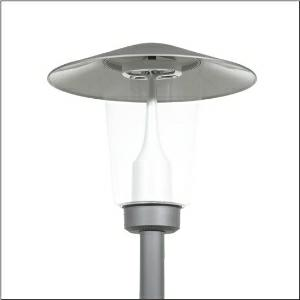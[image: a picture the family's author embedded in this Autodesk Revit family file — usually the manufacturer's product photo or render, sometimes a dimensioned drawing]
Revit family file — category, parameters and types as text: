
# Revit family: pilzleuchte_iq___st1_2a_5xa5235kf14hp_bd7e
name_source: partatom
category: Lighting Fixtures
units: mm (PartAtom-declared; Revit-internal decimal feet)

## family parameters
Cut with Voids When Loaded = No
Host = Face
Light Source = No
Part Type = Normal
Room Calculation Point = No
Round Connector Dimension = Use Diameter
Shared = No

## types (1)
- --- (1 x LED, 4990 lm, 33.6 W, 4000K)
    Apparent Load = 34 VA
    CIE Flux Codes = 23 60 92 98 100
    Color Rendering = 70
    Color Temperature = 4000K
    Default Elevation = 1800 mm
    Description = Mushroom Luminaire iQ, mast luminaire, Module 540 iQ-SR, primary light control with 3 zone facetted reflector, of plastic, silver coated, highly specular, structured, primary optical cover: cover, of PMMA, transparent, light distribution: ST1.2a, light emission: direct distribution, primary light characteristic: asymmetric, installation type: post-top, LED, High Power LED, rated luminous flux: 4.990lm, luminous efficacy: 149lm/W, light colour: 740, colour temperature: 4000K, control gear: iQ Street-Remote, control: pre-setting: logarithmic dimming characteristic, Street-Remote, Auto-Match, Temp-Guard, Lumen-Switch, Night-Set, Smart-Wire, Light-Fading, Desk-Remote (wireless, voltage-free reading and setting of iQ features in the workshop via application-optimized NFC function/RFID function), optimised constant luminous flux control (CLO 2.0), with terminal, 6-pole, max. 2.5mm², mains connection: 230..240V, AC, 50/60Hz, start of lifetime: 34W, end of service life: 36W, reduction: 15W, luminaire housing, upper part, of glass-fibre reinforced polyester, coated, Siteco® metallic grey (DB 702S), diameter: 650mm, height: 586mm, spigot size: d x l = 76 x 70mm (post-top) | with reducer (optional accessory) 60 x 70mm, mounting height: 3..5m, post-top mast mounting element, of diecast aluminium, coated, Siteco® metallic grey (DB 702S), Module 540 iQ-SR, traffic white (RAL 9016), equipment: Power, protection rating (complete): IP65, insulation class (complete): insulation class II (safety insulation), certification: CE, ENEC, VDE, packaging unit: 1 piece

Light Distribution: ST1.2a
    Height = 586 mm
    Lamp = 1 x LED
    Lamp Light Flux = 4990 lm
    Lamp Power = 33.6 W
    Lamp count = 1
    Length = 650 mm
    Luminous efficacy = 149 lm/W
    Manufacturer = Siteco
    ModVariant = No
    Model = 5XA5235KF14HP
    Number of Poles = 1
    OnlyDefault = Yes
    Power Factor = 1
    Product Name = Pilzleuchte iQ | ST1.2a
    Product group = mast luminaire | pylon top
    ProductGroupID = 6100
    Protection Class = Protection class II
    Protection Degree = IP 65
    RLX_Detail_Level = 1
    RLX_Emergency_Light_Flux = 0 lm
    RLX_Emergency_Type = 0
    RLX_Emergency_Type_DB = No
    RlxData = <blob elided: 51445 chars, md5=9f0eccc7>
    Socket = socket
    Standby Power = 0 W
    System Light Flux = 4990 lm
    System Power = 34 W
    Type Comments = factory setting: luminous flux: 100 % | dim-lin: 254 | 695 mA
    Type Image = l_1006077.jpg
    URL = http://relux.com
    VarID = @adj_191047
    Voltage = 0 V
    Weight = 0.00 kg
    Width = 0 mm  [stored 0 ft]

note: [stored X ft] marks values corroborated as IEEE doubles in the binary element streams (Revit-internal decimal feet)

## geometry (parser evidence)
native form markers: Blend x4, Sweep x12
no freeform markers — native parametric forms only
